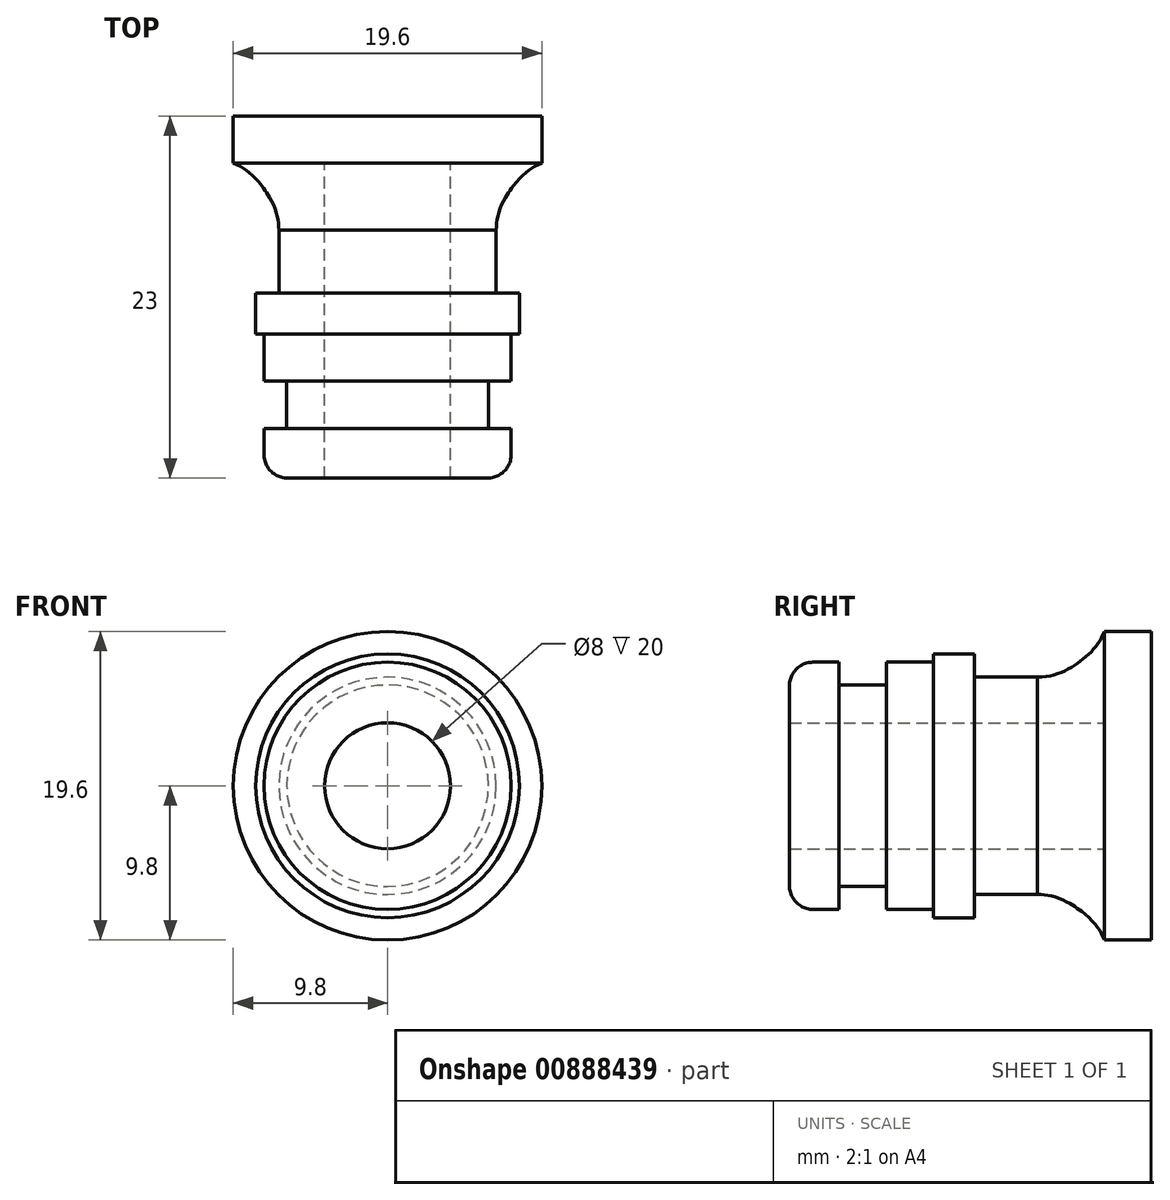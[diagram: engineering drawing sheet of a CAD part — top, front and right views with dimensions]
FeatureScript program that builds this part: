
annotation { "Feature Type Name" : "Feature", "Feature Type Description" : "" }
export const myFeature = defineFeature(function(context is Context, id is Id, definition is map)
    precondition{}
    {
        {
            var Q0;
            Q0=qCreatedBy(makeId("Top.planeOp"),FACE);
            var sketch = newSketch(context, id + "F0", { "sketchPlane" : qUnion([Q0])});
            skLineSegment(sketch, "E0", {"start": v(6.35, -8.67) * mm, "end": v(4, -8.67) * mm});
            skLineSegment(sketch, "E1", {"start": v(7.85, -2.52) * mm, "end": v(6.4, -2.52) * mm});
            skLineSegment(sketch, "E2", {"start": v(6.4, -2.52) * mm, "end": v(6.4, -5.52) * mm});
            skLineSegment(sketch, "E3", {"start": v(6.4, -5.52) * mm, "end": v(7.85, -5.52) * mm});
            skLineSegment(sketch, "E4.trimOffspring", {"start": v(7.85, -5.52) * mm, "end": v(7.85, -7.17) * mm});
            skLineSegment(sketch, "E5", {"start": v(7.85, -2.52) * mm, "end": v(7.85, 0.48) * mm});
            skLineSegment(sketch, "E6", {"start": v(7.85, 0.48) * mm, "end": v(8.38, 0.48) * mm});
            skLineSegment(sketch, "E7", {"start": v(8.38, 0.48) * mm, "end": v(8.38, 3.08) * mm});
            skLineSegment(sketch, "E8", {"start": v(8.38, 3.08) * mm, "end": v(6.9, 3.08) * mm});
            skLineSegment(sketch, "E9", {"start": v(9.8, 11.33) * mm, "end": v(9.8, 14.33) * mm});
            skLineSegment(sketch, "E10", {"start": v(9.8, 14.33) * mm, "end": v(0, 14.33) * mm});
            skLineSegment(sketch, "E11", {"start": v(4, 11.33) * mm, "end": v(4, -8.67) * mm});
            skLineSegment(sketch, "E12", {"start": v(0, 14.63) * mm, "end": v(0, -11.85) * mm, "construction": true});
            skArc(sketch, "E13.filletArc", {"start": v(6.35, -8.67) * mm, "mid": v(7.41, -8.24) * mm, "end": v(7.85, -7.17) * mm});
            skLineSegment(sketch, "E14", {"start": v(4, 11.33) * mm, "end": v(0, 11.33) * mm});
            skLineSegment(sketch, "E15", {"start": v(0, 11.33) * mm, "end": v(0, 14.33) * mm});
            skLineSegment(sketch, "E16", {"start": v(6.9, 3.08) * mm, "end": v(6.9, 7.08) * mm});
            skFitSpline(sketch, "E17", {"points": [v(6.9, 7.08) * mm, v(7.92, 9.8) * mm, v(9.8, 11.33) * mm], "startDerivative": vector(0.12, 6.67) * mm, "endDerivative": vector(4.78, 1.56) * mm});
            skSolve(sketch);
        }
        {
            var Q0;
            Q0=makeQuery(id+"F0.imprint","IMPRINT",FACE,{"disambiguationData":[TD([[makeQuery(id+"F0.imprint","IMPRINT",EDGE,{"derivedFrom":sQuery(id+"F0.wireOp",EDGE,"E0")}),-1.0]])]});
            var Q1;
            Q1=sQuery(id+"F0.wireOp",EDGE,"E12");
            revolve(context, id + "F1", {"surfaceOperationType" : NewSurfaceOperationType.NEW, "entities" : qUnion([Q0]), "axis" : qUnion([Q1]), "revolveType" : RevolveType.FULL});
        }
    });
